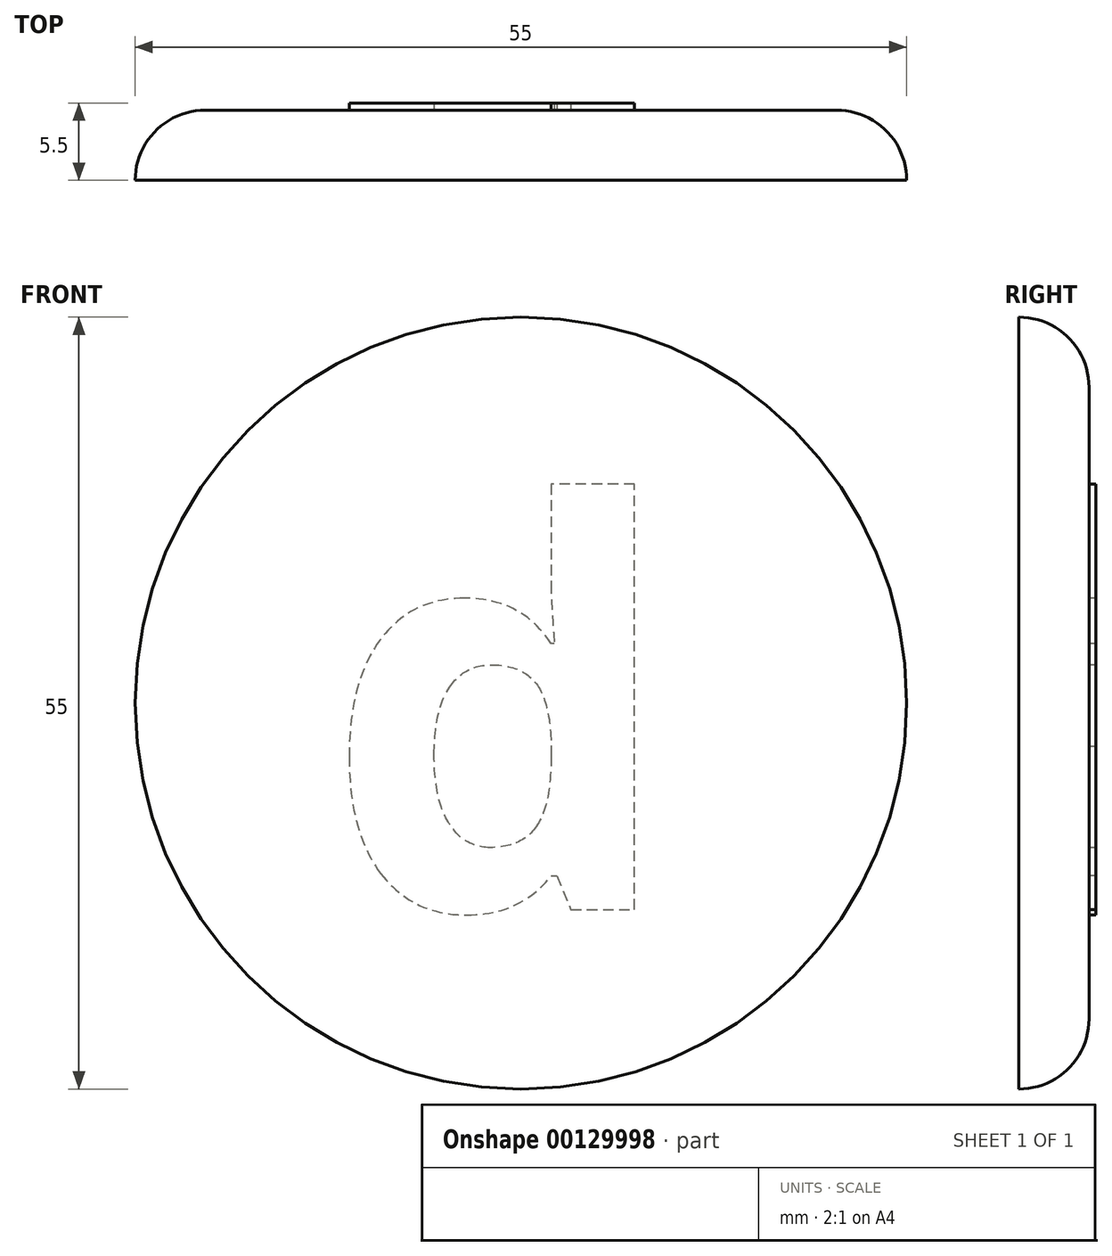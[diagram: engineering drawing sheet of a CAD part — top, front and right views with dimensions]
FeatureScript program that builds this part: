
annotation { "Feature Type Name" : "Feature", "Feature Type Description" : "" }
export const myFeature = defineFeature(function(context is Context, id is Id, definition is map)
    precondition{}
    {
        {
            var Q0;
            Q0=qCreatedBy(makeId("Front.planeOp"),FACE);
            var sketch = newSketch(context, id + "F0", { "sketchPlane" : qUnion([Q0])});
            skCircle(sketch, "E0", {"center": v(-16.18, 22.24) * mm, "radius": 27.5 * mm});
            skSolve(sketch);
        }
        {
            var Q0;
            Q0 = qSketchRegion(id + "F0", true);
            extrude(context, id + "F1", {"entities" : qUnion([Q0]), "depth" : 5 * mm});
        }
        {
            var Q0;
            Q0=makeQuery(id+"F1.opExtrude","CAP_EDGE",EDGE,{"disambiguationData":[OSD([sQuery(id+"F0.wireOp",EDGE,"E0")])],"isStart":true});
            fillet(context, id + "F2", {"entities" : qUnion([Q0]), "radius" : 5 * mm, "tangentPropagation" : true, "allowEdgeOverflow" : false});
        }
        {
            var Q0;
            Q0=makeQuery(id+"F1.opExtrude","CAP_FACE",FACE,{"disambiguationData":[OSD([sQuery(id+"F0.wireOp",EDGE,"E0")])],"isStart":true});
            var sketch = newSketch(context, id + "F3", { "sketchPlane" : qUnion([Q0])});
            skText(sketch, "E1", { "text": "b", "fontName": "OpenSans-Bold.ttf"});
            const initialGuessF3  = {"E1": [0.00497, 0.00753, 1, 0, 0.02872]};
            skSetInitialGuess(sketch, initialGuessF3);
            skSolve(sketch);
        }
        {
            var Q0;
            Q0 = qSketchRegion(id + "F3", true);
            extrude(context, id + "F4", {"entities" : qUnion([Q0]), "operationType" : NewBodyOperationType.ADD, "depth" : 0.5 * mm});
        }
    });
